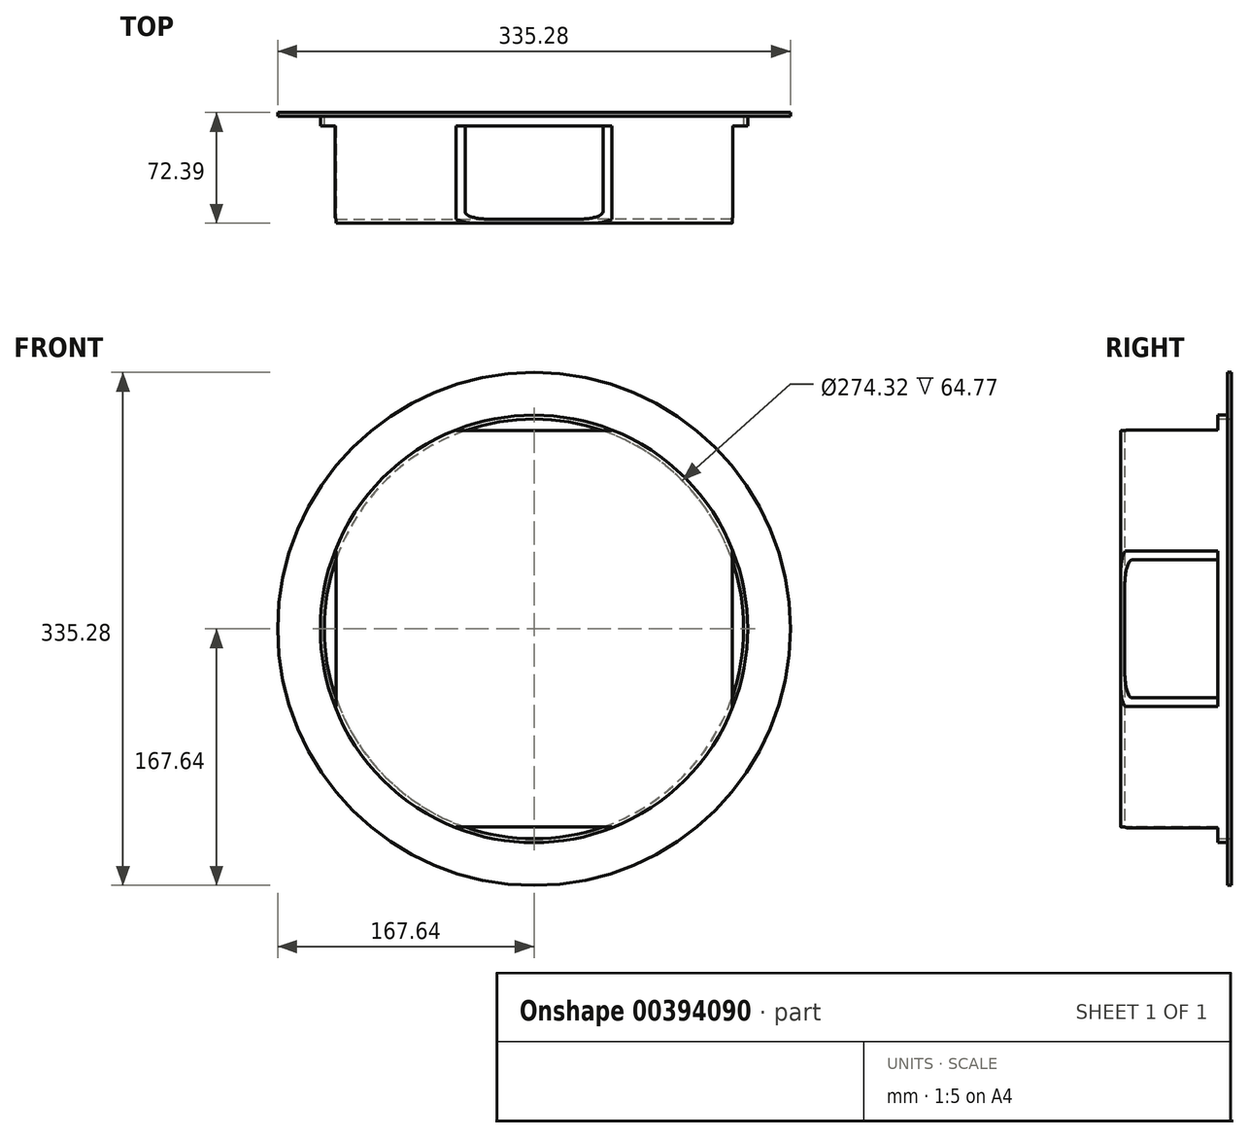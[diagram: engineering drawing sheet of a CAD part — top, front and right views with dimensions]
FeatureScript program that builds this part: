
annotation { "Feature Type Name" : "Feature", "Feature Type Description" : "" }
export const myFeature = defineFeature(function(context is Context, id is Id, definition is map)
    precondition{}
    {
        {
            var Q0;
            Q0=qCreatedBy(makeId("Front.planeOp"),FACE);
            var sketch = newSketch(context, id + "F0", { "sketchPlane" : qUnion([Q0])});
            skCircle(sketch, "E0", {"center": v(0, 0) * mm, "radius": 139.7 * mm});
            skCircle(sketch, "E1", {"center": v(0, 0) * mm, "radius": 167.64 * mm});
            skCircle(sketch, "E2", {"center": v(0, 0) * mm, "radius": 138.43 * mm});
            skSolve(sketch);
        }
        {
            var Q0;
            Q0=makeQuery(id+"F0.imprint","IMPRINT",FACE,{"disambiguationData":[TD([[makeQuery(id+"F0.imprint","IMPRINT",EDGE,{"derivedFrom":sQuery(id+"F0.wireOp",EDGE,"E0")}),1.0]])]});
            var Q1;
            Q1=makeQuery(id+"F0.imprint","IMPRINT",FACE,{"disambiguationData":[TD([[makeQuery(id+"F0.imprint","IMPRINT",EDGE,{"derivedFrom":sQuery(id+"F0.wireOp",EDGE,"E2")}),1.0]])]});
            extrude(context, id + "F1", {"entities" : qUnion([Q0, Q1]), "depth" : 76.2 * mm});
        }
        {
            var Q0;
            Q0=makeQuery(id+"F0.imprint","IMPRINT",FACE,{"disambiguationData":[TD([[makeQuery(id+"F0.imprint","IMPRINT",EDGE,{"derivedFrom":sQuery(id+"F0.wireOp",EDGE,"E0")}),-1.0]])]});
            extrude(context, id + "F2", {"entities" : qUnion([Q0]), "operationType" : NewBodyOperationType.ADD, "depth" : 6.35 * mm});
        }
        {
            var Q0;
            {var subQ0=sQuery(id+"F0.wireOp",EDGE,"E0");Q0=makeQuery(id+"F2.boolean.opBoolean","MERGE",FACE,{"derivedFrom":[makeQuery(id+"F1.opExtrude","CAP_FACE",FACE,{"disambiguationData":[OSD([subQ0])],"isStart":true}),makeQuery(id+"F2.opExtrude","CAP_FACE",FACE,{"disambiguationData":[OSD([subQ0,sQuery(id+"F0.wireOp",EDGE,"E1")])],"isStart":true})]});}
            shell(context, id + "F3", {"entities" : qUnion([Q0]), "thickness" : 2.54 * mm});
        }
        {
            var Q0;
            Q0=makeQuery(id+"F0.imprint","IMPRINT",FACE,{"disambiguationData":[TD([[makeQuery(id+"F0.imprint","IMPRINT",EDGE,{"derivedFrom":sQuery(id+"F0.wireOp",EDGE,"E0")}),-1.0]])]});
            extrude(context, id + "F4", {"entities" : qUnion([Q0]), "operationType" : NewBodyOperationType.REMOVE, "depth" : 3.8 * mm});
        }
        {
            var Q0;
            Q0=makeQuery(id+"F1.opExtrude","CAP_EDGE",EDGE,{"disambiguationData":[OSD([sQuery(id+"F0.wireOp",EDGE,"E0")])],"isStart":false});
            var Q1;
            Q1=makeQuery(id+"F2.opExtrude","CAP_EDGE",EDGE,{"disambiguationData":[OSD([sQuery(id+"F0.wireOp",EDGE,"E0")])],"isStart":false});
            var Q2;
            {var subQ0=sQuery(id+"F0.wireOp",EDGE,"E0");Q2=makeQuery(id+"F3.opShell","OFFSET_EDGE",EDGE,{"disambiguationData":[OSD([subQ0]),TDD([makeQuery(id+"F1.opExtrude","CAP_EDGE",EDGE,{"disambiguationData":[OSD([subQ0])],"isStart":false})])]});}
            fillet(context, id + "F5", {"entities" : qUnion([Q0, Q1, Q2]), "radius" : 5.08 * mm, "tangentPropagation" : true, "allowEdgeOverflow" : false});
        }
        {
            var Q0;
            Q0=makeQuery(id+"F1.opExtrude","CAP_FACE",FACE,{"disambiguationData":[OSD([sQuery(id+"F0.wireOp",EDGE,"E0")])],"isStart":false});
            var sketch = newSketch(context, id + "F6", { "sketchPlane" : qUnion([Q0])});
            skLineSegment(sketch, "E3.bottom", {"start": v(-129.54, -50.8) * mm, "end": v(-139.7, -50.8) * mm});
            skLineSegment(sketch, "E3.top", {"start": v(-129.54, 50.8) * mm, "end": v(-139.7, 50.8) * mm});
            skLineSegment(sketch, "E3.left", {"start": v(-129.54, -50.8) * mm, "end": v(-129.54, 50.8) * mm});
            skLineSegment(sketch, "E3.right", {"start": v(-139.7, -50.8) * mm, "end": v(-139.7, 50.8) * mm});
            skPoint(sketch, "E3.middle", {"position": v(-134.62, 0) * mm});
            skLineSegment(sketch, "E4.MirrorCS", {"start": v(129.54, -50.8) * mm, "end": v(129.54, 50.8) * mm});
            skLineSegment(sketch, "E5.MirrorCS", {"start": v(129.54, 50.8) * mm, "end": v(139.7, 50.8) * mm});
            skLineSegment(sketch, "E6.MirrorCS", {"start": v(139.7, -50.8) * mm, "end": v(139.7, 50.8) * mm});
            skLineSegment(sketch, "E7.MirrorCS", {"start": v(129.54, -50.8) * mm, "end": v(139.7, -50.8) * mm});
            skLineSegment(sketch, "E8.bottom", {"start": v(50.8, 129.54) * mm, "end": v(-50.8, 129.54) * mm});
            skLineSegment(sketch, "E8.top", {"start": v(50.8, 139.7) * mm, "end": v(-50.8, 139.7) * mm});
            skLineSegment(sketch, "E8.left", {"start": v(50.8, 129.54) * mm, "end": v(50.8, 139.7) * mm});
            skLineSegment(sketch, "E8.right", {"start": v(-50.8, 129.54) * mm, "end": v(-50.8, 139.7) * mm});
            skPoint(sketch, "E8.middle", {"position": v(0, 134.62) * mm});
            skLineSegment(sketch, "E9.MirrorCS", {"start": v(50.8, -139.7) * mm, "end": v(-50.8, -139.7) * mm});
            skLineSegment(sketch, "E10.MirrorCS", {"start": v(50.8, -129.54) * mm, "end": v(-50.8, -129.54) * mm});
            skLineSegment(sketch, "E11.MirrorCS", {"start": v(50.8, -129.54) * mm, "end": v(50.8, -139.7) * mm});
            skLineSegment(sketch, "E12.MirrorCS", {"start": v(-50.8, -129.54) * mm, "end": v(-50.8, -139.7) * mm});
            skSolve(sketch);
        }
        {
            var Q0;
            {var subQ5=sQuery(id+"F6.wireOp",EDGE,"E3.bottom");Q0=makeQuery(id+"F6.imprint","IMPRINT",FACE,{"disambiguationData":[TD([[makeQuery(id+"F6.imprint","IMPRINT",EDGE,{"derivedFrom":subQ5}),-1.0]])]});}
            var Q1;
            {var subQ0=sQuery(id+"F6.wireOp",EDGE,"E5.MirrorCS");Q1=makeQuery(id+"F6.imprint","IMPRINT",FACE,{"disambiguationData":[TD([[makeQuery(id+"F6.imprint","IMPRINT",EDGE,{"derivedFrom":subQ0}),-1.0]])]});}
            var Q2;
            {var subQ0=sQuery(id+"F6.wireOp",EDGE,"E3.left");var subQ1=sQuery(id+"F0.wireOp",EDGE,"E0");var subQ2=makeQuery(id+"F5.opFillet","BLEND_EDGE",EDGE,{"blendedFrom":[makeQuery(id+"F1.opExtrude","CAP_EDGE",EDGE,{"disambiguationData":[OSD([subQ1])],"isStart":false}),makeQuery(id+"F1.opExtrude","CAP_FACE",FACE,{"disambiguationData":[OSD([subQ1])],"isStart":false})],"blendedInto":[makeQuery(id+"F1.opExtrude","CAP_FACE",FACE,{"disambiguationData":[OSD([subQ1])],"isStart":false})]});var subQ3=makeQuery(id+"F6.imprint","INTERSECT",VERTEX,{"disambiguationData":[OD(0.0)],"derivedFrom":[subQ2,subQ0]});Q2=makeQuery(id+"F6.imprint","IMPRINT",FACE,{"disambiguationData":[TD([[makeQuery(id+"F6.imprint","IMPRINT",EDGE,{"disambiguationData":[TD([[subQ3,-1.0]])],"derivedFrom":subQ0}),1.0]])]});}
            var Q3;
            {var subQ0=sQuery(id+"F6.wireOp",EDGE,"E4.MirrorCS");var subQ1=sQuery(id+"F0.wireOp",EDGE,"E0");var subQ2=makeQuery(id+"F5.opFillet","BLEND_EDGE",EDGE,{"blendedFrom":[makeQuery(id+"F1.opExtrude","CAP_EDGE",EDGE,{"disambiguationData":[OSD([subQ1])],"isStart":false}),makeQuery(id+"F1.opExtrude","CAP_FACE",FACE,{"disambiguationData":[OSD([subQ1])],"isStart":false})],"blendedInto":[makeQuery(id+"F1.opExtrude","CAP_FACE",FACE,{"disambiguationData":[OSD([subQ1])],"isStart":false})]});var subQ3=makeQuery(id+"F6.imprint","INTERSECT",VERTEX,{"disambiguationData":[OD(0.0)],"derivedFrom":[subQ2,subQ0]});Q3=makeQuery(id+"F6.imprint","IMPRINT",FACE,{"disambiguationData":[TD([[makeQuery(id+"F6.imprint","IMPRINT",EDGE,{"disambiguationData":[TD([[subQ3,-1.0]])],"derivedFrom":subQ0}),-1.0]])]});}
            var Q4;
            Q4=makeQuery(id+"F6.imprint","IMPRINT",FACE,{"disambiguationData":[TD([[makeQuery(id+"F6.imprint","IMPRINT",EDGE,{"derivedFrom":sQuery(id+"F6.wireOp",EDGE,"E8.top")}),1.0]])]});
            var Q5;
            {var subQ0=sQuery(id+"F6.wireOp",EDGE,"E8.bottom");var subQ1=sQuery(id+"F0.wireOp",EDGE,"E0");var subQ2=makeQuery(id+"F5.opFillet","BLEND_EDGE",EDGE,{"blendedFrom":[makeQuery(id+"F1.opExtrude","CAP_EDGE",EDGE,{"disambiguationData":[OSD([subQ1])],"isStart":false}),makeQuery(id+"F1.opExtrude","CAP_FACE",FACE,{"disambiguationData":[OSD([subQ1])],"isStart":false})],"blendedInto":[makeQuery(id+"F1.opExtrude","CAP_FACE",FACE,{"disambiguationData":[OSD([subQ1])],"isStart":false})]});var subQ3=makeQuery(id+"F6.imprint","INTERSECT",VERTEX,{"disambiguationData":[OD(0.0)],"derivedFrom":[subQ2,subQ0]});Q5=makeQuery(id+"F6.imprint","IMPRINT",FACE,{"disambiguationData":[TD([[makeQuery(id+"F6.imprint","IMPRINT",EDGE,{"disambiguationData":[TD([[subQ3,-1.0]])],"derivedFrom":subQ0}),-1.0]])]});}
            var Q6;
            {var subQ0=sQuery(id+"F6.wireOp",EDGE,"E10.MirrorCS");var subQ1=sQuery(id+"F0.wireOp",EDGE,"E0");var subQ2=makeQuery(id+"F5.opFillet","BLEND_EDGE",EDGE,{"blendedFrom":[makeQuery(id+"F1.opExtrude","CAP_EDGE",EDGE,{"disambiguationData":[OSD([subQ1])],"isStart":false}),makeQuery(id+"F1.opExtrude","CAP_FACE",FACE,{"disambiguationData":[OSD([subQ1])],"isStart":false})],"blendedInto":[makeQuery(id+"F1.opExtrude","CAP_FACE",FACE,{"disambiguationData":[OSD([subQ1])],"isStart":false})]});var subQ3=makeQuery(id+"F6.imprint","INTERSECT",VERTEX,{"disambiguationData":[OD(0.0)],"derivedFrom":[subQ2,subQ0]});Q6=makeQuery(id+"F6.imprint","IMPRINT",FACE,{"disambiguationData":[TD([[makeQuery(id+"F6.imprint","IMPRINT",EDGE,{"disambiguationData":[TD([[subQ3,-1.0]])],"derivedFrom":subQ0}),1.0]])]});}
            var Q7;
            Q7=makeQuery(id+"F6.imprint","IMPRINT",FACE,{"disambiguationData":[TD([[makeQuery(id+"F6.imprint","IMPRINT",EDGE,{"derivedFrom":sQuery(id+"F6.wireOp",EDGE,"E9.MirrorCS")}),-1.0]])]});
            extrude(context, id + "F7", {"entities" : qUnion([Q0, Q1, Q2, Q3, Q4, Q5, Q6, Q7]), "operationType" : NewBodyOperationType.REMOVE, "oppositeDirection" : true, "depth" : 63.5 * mm});
        }
    });
